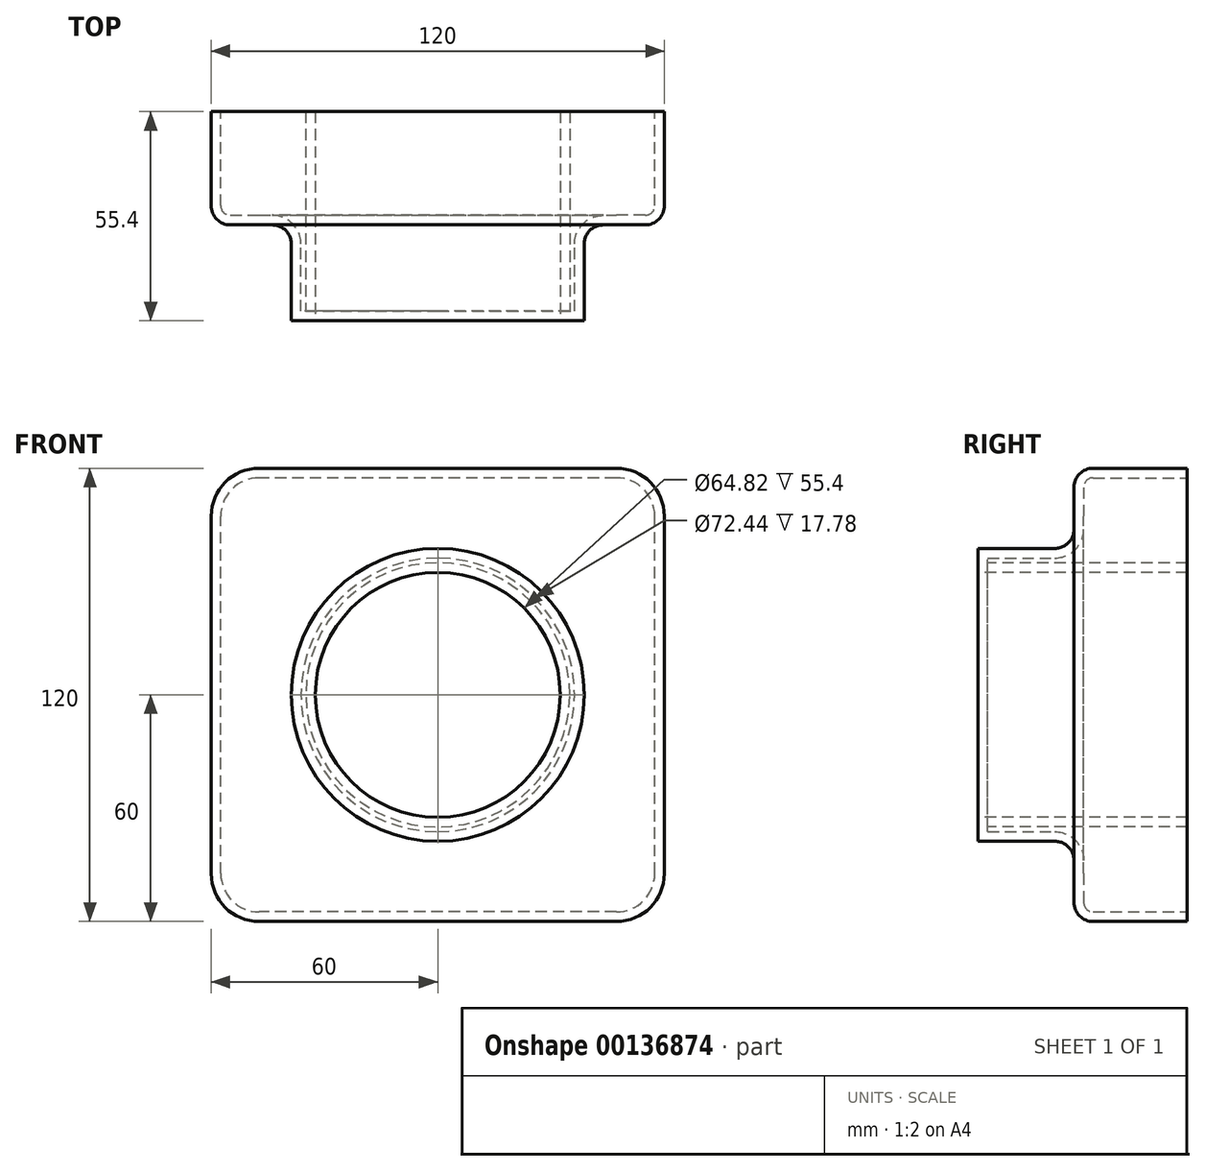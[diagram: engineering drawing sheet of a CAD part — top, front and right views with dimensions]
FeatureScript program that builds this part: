
annotation { "Feature Type Name" : "Feature", "Feature Type Description" : "" }
export const myFeature = defineFeature(function(context is Context, id is Id, definition is map)
    precondition{}
    {
        {
            var Q0;
            Q0=qCreatedBy(makeId("Front.planeOp"),FACE);
            var sketch = newSketch(context, id + "F0", { "sketchPlane" : qUnion([Q0])});
            skLineSegment(sketch, "E0.bottom", {"start": v(60, -60) * mm, "end": v(-60, -60) * mm});
            skLineSegment(sketch, "E0.top", {"start": v(60, 60) * mm, "end": v(-60, 60) * mm});
            skLineSegment(sketch, "E0.left", {"start": v(60, -60) * mm, "end": v(60, 60) * mm});
            skLineSegment(sketch, "E0.right", {"start": v(-60, -60) * mm, "end": v(-60, 60) * mm});
            skPoint(sketch, "E0.middle", {"position": v(0, 0) * mm});
            skSolve(sketch);
        }
        {
            var Q0;
            Q0 = qSketchRegion(id + "F0", true);
            extrude(context, id + "F1", {"entities" : qUnion([Q0]), "depth" : 30 * mm});
        }
        {
            var Q0;
            Q0=makeQuery(id+"F1.opExtrude","CAP_FACE",FACE,{"disambiguationData":[OSD([sQuery(id+"F0.wireOp",EDGE,"E0.bottom"),sQuery(id+"F0.wireOp",EDGE,"E0.top"),sQuery(id+"F0.wireOp",EDGE,"E0.left"),sQuery(id+"F0.wireOp",EDGE,"E0.right")])],"isStart":false});
            var sketch = newSketch(context, id + "F2", { "sketchPlane" : qUnion([Q0])});
            skCircle(sketch, "E1", {"center": v(0, 0) * mm, "radius": 38.76 * mm});
            skSolve(sketch);
        }
        {
            var Q0;
            Q0 = qSketchRegion(id + "F2", true);
            extrude(context, id + "F3", {"entities" : qUnion([Q0]), "operationType" : NewBodyOperationType.ADD, "depth" : 25.4 * mm});
        }
        {
            var Q0;
            Q0=makeQuery(id+"F3.opExtrude","CAP_FACE",FACE,{"disambiguationData":[OSD([sQuery(id+"F2.wireOp",EDGE,"E1")])],"isStart":false});
            var sketch = newSketch(context, id + "F4", { "sketchPlane" : qUnion([Q0])});
            skCircle(sketch, "E2.0", {"center": v(0, 0) * mm, "radius": 32.41 * mm});
            skSolve(sketch);
        }
        {
            var Q0;
            Q0=makeQuery(id+"F4.imprint","IMPRINT",FACE,{"disambiguationData":[TD([[makeQuery(id+"F4.imprint","IMPRINT",EDGE,{"derivedFrom":sQuery(id+"F4.wireOp",EDGE,"E2.0")}),1.0]])]});
            extrude(context, id + "F5", {"entities" : qUnion([Q0]), "operationType" : NewBodyOperationType.REMOVE, "endBound" : BoundingType.THROUGH_ALL, "oppositeDirection" : true, "depth" : 25.4 * mm});
        }
        {
            var Q0;
            Q0=makeQuery(id+"F1.opExtrude","SWEPT_EDGE",EDGE,{"disambiguationData":[OSD([sQuery(id+"F0.wireOp",EDGE,"E0.bottom"),sQuery(id+"F0.wireOp",EDGE,"E0.right")])]});
            var Q1;
            Q1=makeQuery(id+"F1.opExtrude","SWEPT_EDGE",EDGE,{"disambiguationData":[OSD([sQuery(id+"F0.wireOp",EDGE,"E0.top"),sQuery(id+"F0.wireOp",EDGE,"E0.right")])]});
            var Q2;
            Q2=makeQuery(id+"F1.opExtrude","SWEPT_EDGE",EDGE,{"disambiguationData":[OSD([sQuery(id+"F0.wireOp",EDGE,"E0.top"),sQuery(id+"F0.wireOp",EDGE,"E0.left")])]});
            var Q3;
            Q3=makeQuery(id+"F1.opExtrude","SWEPT_EDGE",EDGE,{"disambiguationData":[OSD([sQuery(id+"F0.wireOp",EDGE,"E0.bottom"),sQuery(id+"F0.wireOp",EDGE,"E0.left")])]});
            fillet(context, id + "F6", {"entities" : qUnion([Q0, Q1, Q2, Q3]), "radius" : 12.7 * mm, "tangentPropagation" : true, "allowEdgeOverflow" : false});
        }
        {
            var Q0;
            Q0=makeQuery(id+"F1.opExtrude","CAP_FACE",FACE,{"disambiguationData":[OSD([sQuery(id+"F0.wireOp",EDGE,"E0.bottom"),sQuery(id+"F0.wireOp",EDGE,"E0.top"),sQuery(id+"F0.wireOp",EDGE,"E0.left"),sQuery(id+"F0.wireOp",EDGE,"E0.right")])],"isStart":false});
            fillet(context, id + "F7", {"entities" : qUnion([Q0]), "radius" : 5.08 * mm, "tangentPropagation" : true, "allowEdgeOverflow" : false});
        }
        {
            var Q0;
            Q0=makeQuery(id+"F1.opExtrude","CAP_FACE",FACE,{"disambiguationData":[OSD([sQuery(id+"F0.wireOp",EDGE,"E0.bottom"),sQuery(id+"F0.wireOp",EDGE,"E0.top"),sQuery(id+"F0.wireOp",EDGE,"E0.left"),sQuery(id+"F0.wireOp",EDGE,"E0.right")])],"isStart":true});
            shell(context, id + "F8", {"entities" : qUnion([Q0]), "thickness" : 2.54 * mm});
        }
    });
